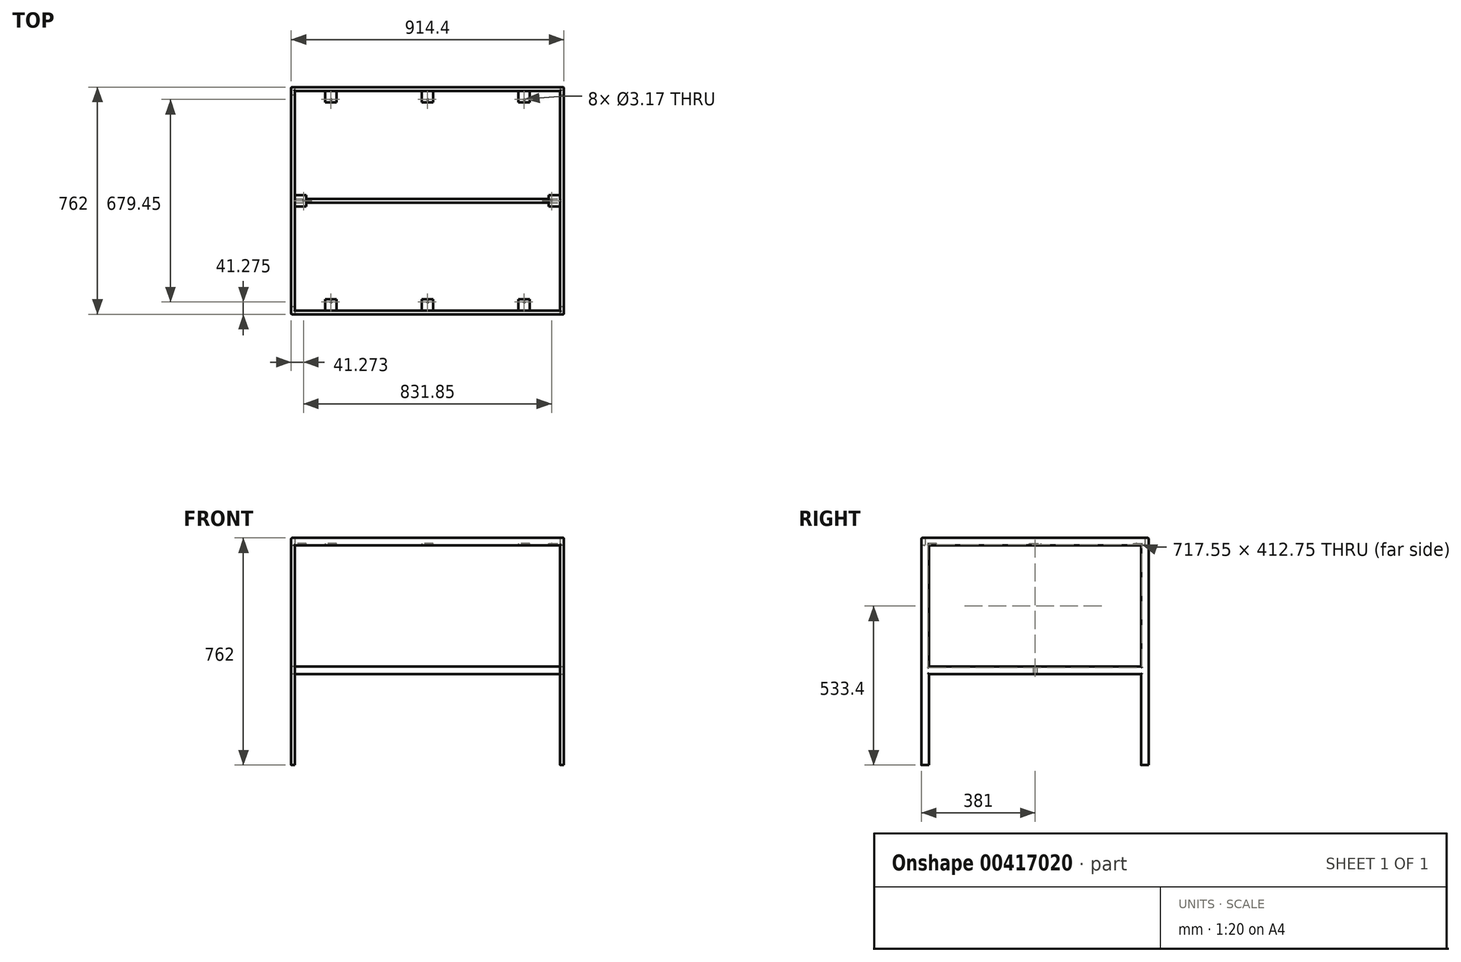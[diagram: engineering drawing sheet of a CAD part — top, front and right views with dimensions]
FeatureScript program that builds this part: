
annotation { "Feature Type Name" : "Feature", "Feature Type Description" : "" }
export const myFeature = defineFeature(function(context is Context, id is Id, definition is map)
    precondition{}
    {
        {
            var Q0;
            Q0=qCreatedBy(makeId("Top.planeOp"),FACE);
            var sketch = newSketch(context, id + "F0", { "sketchPlane" : qUnion([Q0])});
            skLineSegment(sketch, "E0.bottom", {"start": v(-452.22, 494.84) * mm, "end": v(462.18, 494.84) * mm});
            skLineSegment(sketch, "E0.top", {"start": v(-452.22, -267.16) * mm, "end": v(462.18, -267.16) * mm});
            skLineSegment(sketch, "E0.left", {"start": v(-452.22, 494.84) * mm, "end": v(-452.22, -267.16) * mm});
            skLineSegment(sketch, "E0.right", {"start": v(462.18, 494.84) * mm, "end": v(462.18, -267.16) * mm});
            skLineSegment(sketch, "E1.bottom", {"start": v(-439.52, 482.14) * mm, "end": v(449.48, 482.14) * mm});
            skLineSegment(sketch, "E1.top", {"start": v(-439.52, -254.46) * mm, "end": v(449.48, -254.46) * mm});
            skLineSegment(sketch, "E1.left", {"start": v(-439.52, 482.14) * mm, "end": v(-439.52, -254.46) * mm});
            skLineSegment(sketch, "E1.right", {"start": v(449.48, 482.14) * mm, "end": v(449.48, -254.46) * mm});
            skSolve(sketch);
        }
        {
            var Q0;
            Q0=makeQuery(id+"F0.imprint","IMPRINT",FACE,{"disambiguationData":[TD([[makeQuery(id+"F0.imprint","IMPRINT",EDGE,{"derivedFrom":sQuery(id+"F0.wireOp",EDGE,"E0.bottom")}),-1.0]])]});
            extrude(context, id + "F1", {"entities" : qUnion([Q0]), "depth" : 25.4 * mm});
        }
        {
            var Q0;
            Q0=makeQuery(id+"F1.opExtrude","CAP_FACE",FACE,{"disambiguationData":[OSD([sQuery(id+"F0.wireOp",EDGE,"E0.bottom"),sQuery(id+"F0.wireOp",EDGE,"E0.top"),sQuery(id+"F0.wireOp",EDGE,"E0.left"),sQuery(id+"F0.wireOp",EDGE,"E0.right"),sQuery(id+"F0.wireOp",EDGE,"E1.bottom"),sQuery(id+"F0.wireOp",EDGE,"E1.top"),sQuery(id+"F0.wireOp",EDGE,"E1.left"),sQuery(id+"F0.wireOp",EDGE,"E1.right")])],"isStart":true});
            var sketch = newSketch(context, id + "F2", { "sketchPlane" : qUnion([Q0])});
            skLineSegment(sketch, "E2.bottom", {"start": v(-452.22, 267.16) * mm, "end": v(-439.52, 267.16) * mm});
            skLineSegment(sketch, "E2.top", {"start": v(-452.22, 241.76) * mm, "end": v(-439.52, 241.76) * mm});
            skLineSegment(sketch, "E2.left", {"start": v(-452.22, 267.16) * mm, "end": v(-452.22, 241.76) * mm});
            skLineSegment(sketch, "E2.right", {"start": v(-439.52, 267.16) * mm, "end": v(-439.52, 241.76) * mm});
            skLineSegment(sketch, "E3.bottom", {"start": v(-452.22, -494.84) * mm, "end": v(-439.52, -494.84) * mm});
            skLineSegment(sketch, "E3.top", {"start": v(-452.22, -469.44) * mm, "end": v(-439.52, -469.44) * mm});
            skLineSegment(sketch, "E3.left", {"start": v(-452.22, -494.84) * mm, "end": v(-452.22, -469.44) * mm});
            skLineSegment(sketch, "E3.right", {"start": v(-439.52, -494.84) * mm, "end": v(-439.52, -469.44) * mm});
            skLineSegment(sketch, "E4.bottom", {"start": v(462.18, -494.84) * mm, "end": v(449.48, -494.84) * mm});
            skLineSegment(sketch, "E4.top", {"start": v(462.18, -469.44) * mm, "end": v(449.48, -469.44) * mm});
            skLineSegment(sketch, "E4.left", {"start": v(462.18, -494.84) * mm, "end": v(462.18, -469.44) * mm});
            skLineSegment(sketch, "E4.right", {"start": v(449.48, -494.84) * mm, "end": v(449.48, -469.44) * mm});
            skLineSegment(sketch, "E5.bottom", {"start": v(462.18, 267.16) * mm, "end": v(449.48, 267.16) * mm});
            skLineSegment(sketch, "E5.top", {"start": v(462.18, 241.76) * mm, "end": v(449.48, 241.76) * mm});
            skLineSegment(sketch, "E5.left", {"start": v(462.18, 267.16) * mm, "end": v(462.18, 241.76) * mm});
            skLineSegment(sketch, "E5.right", {"start": v(449.48, 267.16) * mm, "end": v(449.48, 241.76) * mm});
            skSolve(sketch);
        }
        {
            var Q0;
            {var subQ2=sQuery(id+"F2.wireOp",EDGE,"E2.bottom");Q0=makeQuery(id+"F2.imprint","IMPRINT",FACE,{"disambiguationData":[TD([[makeQuery(id+"F2.imprint","IMPRINT",EDGE,{"derivedFrom":subQ2}),-1.0]])]});}
            var Q1;
            {var subQ3=sQuery(id+"F2.wireOp",EDGE,"E3.bottom");Q1=makeQuery(id+"F2.imprint","IMPRINT",FACE,{"disambiguationData":[TD([[makeQuery(id+"F2.imprint","IMPRINT",EDGE,{"derivedFrom":subQ3}),1.0]])]});}
            var Q2;
            {var subQ3=sQuery(id+"F2.wireOp",EDGE,"E4.bottom");Q2=makeQuery(id+"F2.imprint","IMPRINT",FACE,{"disambiguationData":[TD([[makeQuery(id+"F2.imprint","IMPRINT",EDGE,{"derivedFrom":subQ3}),1.0]])]});}
            var Q3;
            {var subQ2=sQuery(id+"F2.wireOp",EDGE,"E5.bottom");Q3=makeQuery(id+"F2.imprint","IMPRINT",FACE,{"disambiguationData":[TD([[makeQuery(id+"F2.imprint","IMPRINT",EDGE,{"derivedFrom":subQ2}),-1.0]])]});}
            extrude(context, id + "F3", {"entities" : qUnion([Q0, Q1, Q2, Q3]), "operationType" : NewBodyOperationType.ADD, "depth" : 736.6 * mm});
        }
        {
            var Q0;
            Q0=makeQuery(id+"F3.boolean.opBoolean","MERGE",FACE,{"derivedFrom":[makeQuery(id+"F1.opExtrude","SWEPT_FACE",FACE,{"disambiguationData":[OSD([sQuery(id+"F0.wireOp",EDGE,"E0.right")])]}),makeQuery(id+"F3.opExtrude","SWEPT_FACE",FACE,{"disambiguationData":[OSD([sQuery(id+"F2.wireOp",EDGE,"E4.left")])]}),makeQuery(id+"F3.opExtrude","SWEPT_FACE",FACE,{"disambiguationData":[OSD([sQuery(id+"F2.wireOp",EDGE,"E5.left")])]})]});
            var sketch = newSketch(context, id + "F4", { "sketchPlane" : qUnion([Q0])});
            skLineSegment(sketch, "E6", {"start": v(-241.76, -406.4) * mm, "end": v(469.44, -406.4) * mm});
            skLineSegment(sketch, "E7", {"start": v(-241.76, -431.8) * mm, "end": v(469.44, -431.8) * mm});
            skSolve(sketch);
        }
        {
            var Q0;
            Q0 = qSketchRegion(id + "F4", true);
            var Q1;
            {var subQ0=sQuery(id+"F4.wireOp",EDGE,"E6");Q1=makeQuery(id+"F4.imprint","IMPRINT",FACE,{"disambiguationData":[TD([[makeQuery(id+"F4.imprint","IMPRINT",EDGE,{"derivedFrom":subQ0}),-1.0]])]});}
            extrude(context, id + "F5", {"entities" : qUnion([Q0, Q1]), "operationType" : NewBodyOperationType.ADD, "depth" : -12.7 * mm});
        }
        {
            var Q0;
            Q0=makeQuery(id+"F3.boolean.opBoolean","MERGE",FACE,{"derivedFrom":[makeQuery(id+"F1.opExtrude","SWEPT_FACE",FACE,{"disambiguationData":[OSD([sQuery(id+"F0.wireOp",EDGE,"E0.left")])]}),makeQuery(id+"F3.opExtrude","SWEPT_FACE",FACE,{"disambiguationData":[OSD([sQuery(id+"F2.wireOp",EDGE,"E2.left")])]}),makeQuery(id+"F3.opExtrude","SWEPT_FACE",FACE,{"disambiguationData":[OSD([sQuery(id+"F2.wireOp",EDGE,"E3.left")])]})]});
            var sketch = newSketch(context, id + "F6", { "sketchPlane" : qUnion([Q0])});
            skLineSegment(sketch, "E8", {"start": v(-469.44, -406.4) * mm, "end": v(241.76, -406.4) * mm});
            skLineSegment(sketch, "E9", {"start": v(-469.44, -431.8) * mm, "end": v(241.76, -431.8) * mm});
            skSolve(sketch);
        }
        {
            var Q0;
            Q0 = qSketchRegion(id + "F6", true);
            var Q1;
            {var subQ0=sQuery(id+"F6.wireOp",EDGE,"E8");Q1=makeQuery(id+"F6.imprint","IMPRINT",FACE,{"disambiguationData":[TD([[makeQuery(id+"F6.imprint","IMPRINT",EDGE,{"derivedFrom":subQ0}),-1.0]])]});}
            extrude(context, id + "F7", {"entities" : qUnion([Q0, Q1]), "operationType" : NewBodyOperationType.ADD, "depth" : -12.7 * mm});
        }
        {
            var Q0;
            Q0=makeQuery(id+"F7.opExtrude","SWEPT_FACE",FACE,{"disambiguationData":[OSD([sQuery(id+"F6.wireOp",EDGE,"E9")])]});
            var sketch = newSketch(context, id + "F8", { "sketchPlane" : qUnion([Q0])});
            skLineSegment(sketch, "E10", {"start": v(-439.52, -107.49) * mm, "end": v(449.48, -107.49) * mm});
            skLineSegment(sketch, "E11", {"start": v(-439.52, -120.19) * mm, "end": v(449.48, -120.19) * mm});
            skLineSegment(sketch, "E12", {"start": v(449.48, -107.49) * mm, "end": v(449.48, -120.19) * mm});
            skSolve(sketch);
        }
        {
            var Q0;
            Q0 = qSketchRegion(id + "F8", true);
            var Q1;
            {var subQ0=sQuery(id+"F8.wireOp",EDGE,"E10");Q1=makeQuery(id+"F8.imprint","IMPRINT",FACE,{"disambiguationData":[TD([[makeQuery(id+"F8.imprint","IMPRINT",EDGE,{"derivedFrom":subQ0}),-1.0]])]});}
            extrude(context, id + "F9", {"entities" : qUnion([Q0, Q1]), "operationType" : NewBodyOperationType.ADD, "depth" : -25.4 * mm});
        }
        {
            var Q0;
            Q0=makeQuery(id+"F1.opExtrude","SWEPT_FACE",FACE,{"disambiguationData":[OSD([sQuery(id+"F0.wireOp",EDGE,"E1.top")])]});
            var sketch = newSketch(context, id + "F10", { "sketchPlane" : qUnion([Q0])});
            skLineSegment(sketch, "E13", {"start": v(-347.88, 0) * mm, "end": v(-347.88, 6.35) * mm});
            skLineSegment(sketch, "E14", {"start": v(-347.88, 6.35) * mm, "end": v(-309.78, 6.35) * mm});
            skLineSegment(sketch, "E15", {"start": v(-309.78, 6.35) * mm, "end": v(-309.78, 0) * mm});
            skLineSegment(sketch, "E16", {"start": v(299.82, 0) * mm, "end": v(299.82, 6.35) * mm});
            skLineSegment(sketch, "E17", {"start": v(299.82, 6.35) * mm, "end": v(337.92, 6.35) * mm});
            skLineSegment(sketch, "E18", {"start": v(337.92, 6.35) * mm, "end": v(337.92, 0) * mm});
            skLineSegment(sketch, "E19", {"start": v(-24.03, 0) * mm, "end": v(-24.03, 6.35) * mm});
            skLineSegment(sketch, "E20", {"start": v(-24.03, 6.35) * mm, "end": v(14.07, 6.35) * mm});
            skLineSegment(sketch, "E21", {"start": v(14.07, 6.35) * mm, "end": v(14.07, 0) * mm});
            skSolve(sketch);
        }
        {
            var Q0;
            Q0 = qSketchRegion(id + "F10", true);
            var Q1;
            {var subQ0=sQuery(id+"F10.wireOp",EDGE,"E19");Q1=makeQuery(id+"F10.imprint","IMPRINT",FACE,{"disambiguationData":[TD([[makeQuery(id+"F10.imprint","IMPRINT",EDGE,{"derivedFrom":subQ0}),-1.0]])]});}
            var Q2;
            {var subQ0=sQuery(id+"F10.wireOp",EDGE,"E13");Q2=makeQuery(id+"F10.imprint","IMPRINT",FACE,{"disambiguationData":[TD([[makeQuery(id+"F10.imprint","IMPRINT",EDGE,{"derivedFrom":subQ0}),-1.0]])]});}
            var Q3;
            {var subQ0=sQuery(id+"F10.wireOp",EDGE,"E16");Q3=makeQuery(id+"F10.imprint","IMPRINT",FACE,{"disambiguationData":[TD([[makeQuery(id+"F10.imprint","IMPRINT",EDGE,{"derivedFrom":subQ0}),-1.0]])]});}
            extrude(context, id + "F11", {"entities" : qUnion([Q0, Q1, Q2, Q3]), "operationType" : NewBodyOperationType.ADD, "depth" : 38.1 * mm});
        }
        {
            var Q0;
            Q0=makeQuery(id+"F1.opExtrude","SWEPT_FACE",FACE,{"disambiguationData":[OSD([sQuery(id+"F0.wireOp",EDGE,"E1.bottom")])]});
            var sketch = newSketch(context, id + "F12", { "sketchPlane" : qUnion([Q0])});
            skLineSegment(sketch, "E22", {"start": v(-337.92, 0) * mm, "end": v(-337.92, 6.35) * mm});
            skLineSegment(sketch, "E23", {"start": v(-337.92, 6.35) * mm, "end": v(-299.82, 6.35) * mm});
            skLineSegment(sketch, "E24", {"start": v(-299.82, 6.35) * mm, "end": v(-299.82, 0) * mm});
            skLineSegment(sketch, "E25", {"start": v(-14.07, 0) * mm, "end": v(-14.07, 6.35) * mm});
            skLineSegment(sketch, "E26", {"start": v(-14.07, 6.35) * mm, "end": v(24.03, 6.35) * mm});
            skLineSegment(sketch, "E27", {"start": v(24.03, 6.35) * mm, "end": v(24.03, 0) * mm});
            skLineSegment(sketch, "E28", {"start": v(309.78, 0) * mm, "end": v(309.78, 6.35) * mm});
            skLineSegment(sketch, "E29", {"start": v(309.78, 6.35) * mm, "end": v(347.88, 6.35) * mm});
            skLineSegment(sketch, "E30", {"start": v(347.88, 6.35) * mm, "end": v(347.88, 0) * mm});
            skSolve(sketch);
        }
        {
            var Q0;
            {var subQ0=sQuery(id+"F12.wireOp",EDGE,"E22");Q0=makeQuery(id+"F12.imprint","IMPRINT",FACE,{"disambiguationData":[TD([[makeQuery(id+"F12.imprint","IMPRINT",EDGE,{"derivedFrom":subQ0}),-1.0]])]});}
            var Q1;
            {var subQ0=sQuery(id+"F12.wireOp",EDGE,"E25");Q1=makeQuery(id+"F12.imprint","IMPRINT",FACE,{"disambiguationData":[TD([[makeQuery(id+"F12.imprint","IMPRINT",EDGE,{"derivedFrom":subQ0}),-1.0]])]});}
            var Q2;
            {var subQ0=sQuery(id+"F12.wireOp",EDGE,"E28");Q2=makeQuery(id+"F12.imprint","IMPRINT",FACE,{"disambiguationData":[TD([[makeQuery(id+"F12.imprint","IMPRINT",EDGE,{"derivedFrom":subQ0}),-1.0]])]});}
            extrude(context, id + "F13", {"entities" : qUnion([Q0, Q1, Q2]), "operationType" : NewBodyOperationType.ADD, "depth" : 38.1 * mm});
        }
        {
            var Q0;
            Q0=makeQuery(id+"F7.boolean.opBoolean","MERGE",FACE,{"derivedFrom":[makeQuery(id+"F3.boolean.opBoolean","MERGE",FACE,{"derivedFrom":[makeQuery(id+"F1.opExtrude","SWEPT_FACE",FACE,{"disambiguationData":[OSD([sQuery(id+"F0.wireOp",EDGE,"E1.left")])]}),makeQuery(id+"F3.opExtrude","SWEPT_FACE",FACE,{"disambiguationData":[OSD([sQuery(id+"F2.wireOp",EDGE,"E2.right")])]}),makeQuery(id+"F3.opExtrude","SWEPT_FACE",FACE,{"disambiguationData":[OSD([sQuery(id+"F2.wireOp",EDGE,"E3.right")])]})]}),makeQuery(id+"F7.opExtrude","CAP_FACE",FACE,{"disambiguationData":[OSD([sQuery(id+"F0.wireOp",EDGE,"E0.left"),sQuery(id+"F2.wireOp",EDGE,"E2.top"),sQuery(id+"F2.wireOp",EDGE,"E2.left"),sQuery(id+"F2.wireOp",EDGE,"E3.top"),sQuery(id+"F2.wireOp",EDGE,"E3.left"),sQuery(id+"F6.wireOp",EDGE,"E8"),sQuery(id+"F6.wireOp",EDGE,"E9")])],"isStart":false})]});
            var sketch = newSketch(context, id + "F14", { "sketchPlane" : qUnion([Q0])});
            skLineSegment(sketch, "E31", {"start": v(94.79, 0) * mm, "end": v(94.79, 6.35) * mm});
            skLineSegment(sketch, "E32", {"start": v(94.79, 6.35) * mm, "end": v(132.89, 6.35) * mm});
            skLineSegment(sketch, "E33", {"start": v(132.89, 6.35) * mm, "end": v(132.89, 0) * mm});
            skSolve(sketch);
        }
        {
            var Q0;
            Q0 = qSketchRegion(id + "F14", true);
            var Q1;
            {var subQ0=sQuery(id+"F14.wireOp",EDGE,"E31");Q1=makeQuery(id+"F14.imprint","IMPRINT",FACE,{"disambiguationData":[TD([[makeQuery(id+"F14.imprint","IMPRINT",EDGE,{"derivedFrom":subQ0}),-1.0]])]});}
            extrude(context, id + "F15", {"entities" : qUnion([Q0, Q1]), "operationType" : NewBodyOperationType.ADD, "depth" : 38.1 * mm});
        }
        {
            var Q0;
            Q0=makeQuery(id+"F5.boolean.opBoolean","MERGE",FACE,{"derivedFrom":[makeQuery(id+"F3.boolean.opBoolean","MERGE",FACE,{"derivedFrom":[makeQuery(id+"F1.opExtrude","SWEPT_FACE",FACE,{"disambiguationData":[OSD([sQuery(id+"F0.wireOp",EDGE,"E1.right")])]}),makeQuery(id+"F3.opExtrude","SWEPT_FACE",FACE,{"disambiguationData":[OSD([sQuery(id+"F2.wireOp",EDGE,"E4.right")])]}),makeQuery(id+"F3.opExtrude","SWEPT_FACE",FACE,{"disambiguationData":[OSD([sQuery(id+"F2.wireOp",EDGE,"E5.right")])]})]}),makeQuery(id+"F5.opExtrude","CAP_FACE",FACE,{"disambiguationData":[OSD([sQuery(id+"F0.wireOp",EDGE,"E0.right"),sQuery(id+"F2.wireOp",EDGE,"E4.top"),sQuery(id+"F2.wireOp",EDGE,"E4.left"),sQuery(id+"F2.wireOp",EDGE,"E5.top"),sQuery(id+"F2.wireOp",EDGE,"E5.left"),sQuery(id+"F4.wireOp",EDGE,"E6"),sQuery(id+"F4.wireOp",EDGE,"E7")])],"isStart":false})]});
            var sketch = newSketch(context, id + "F16", { "sketchPlane" : qUnion([Q0])});
            skLineSegment(sketch, "E34", {"start": v(-132.89, 0) * mm, "end": v(-132.89, 6.35) * mm});
            skLineSegment(sketch, "E35", {"start": v(-132.89, 6.35) * mm, "end": v(-94.79, 6.35) * mm});
            skLineSegment(sketch, "E36", {"start": v(-94.79, 6.35) * mm, "end": v(-94.79, 0) * mm});
            skSolve(sketch);
        }
        {
            var Q0;
            {var subQ0=sQuery(id+"F16.wireOp",EDGE,"E34");Q0=makeQuery(id+"F16.imprint","IMPRINT",FACE,{"disambiguationData":[TD([[makeQuery(id+"F16.imprint","IMPRINT",EDGE,{"derivedFrom":subQ0}),-1.0]])]});}
            extrude(context, id + "F17", {"entities" : qUnion([Q0]), "operationType" : NewBodyOperationType.ADD, "depth" : 38.1 * mm});
        }
        {
            var Q0;
            Q0=makeQuery(id+"F13.opExtrude","SWEPT_FACE",FACE,{"disambiguationData":[OSD([sQuery(id+"F12.wireOp",EDGE,"E23")])]});
            var sketch = newSketch(context, id + "F18", { "sketchPlane" : qUnion([Q0])});
            skCircle(sketch, "E37", {"center": v(-318.87, 453.56) * mm, "radius": 1.59 * mm});
            skCircle(sketch, "E38", {"center": v(4.98, 453.56) * mm, "radius": 1.59 * mm});
            skCircle(sketch, "E39", {"center": v(328.83, 453.56) * mm, "radius": 1.59 * mm});
            skCircle(sketch, "E40", {"center": v(-318.87, -225.89) * mm, "radius": 1.59 * mm});
            skCircle(sketch, "E41", {"center": v(4.98, -225.89) * mm, "radius": 1.59 * mm});
            skCircle(sketch, "E42", {"center": v(328.83, -225.89) * mm, "radius": 1.59 * mm});
            skCircle(sketch, "E43", {"center": v(420.9, 113.84) * mm, "radius": 1.59 * mm});
            skCircle(sketch, "E44", {"center": v(-410.95, 113.84) * mm, "radius": 1.59 * mm});
            skSolve(sketch);
        }
        {
            var Q0;
            Q0=makeQuery(id+"F18.imprint","IMPRINT",FACE,{"disambiguationData":[TD([[makeQuery(id+"F18.imprint","IMPRINT",EDGE,{"derivedFrom":sQuery(id+"F18.wireOp",EDGE,"E37")}),1.0]])]});
            var Q1;
            Q1=makeQuery(id+"F18.imprint","IMPRINT",FACE,{"disambiguationData":[TD([[makeQuery(id+"F18.imprint","IMPRINT",EDGE,{"derivedFrom":sQuery(id+"F18.wireOp",EDGE,"E38")}),1.0]])]});
            var Q2;
            Q2=makeQuery(id+"F18.imprint","IMPRINT",FACE,{"disambiguationData":[TD([[makeQuery(id+"F18.imprint","IMPRINT",EDGE,{"derivedFrom":sQuery(id+"F18.wireOp",EDGE,"E39")}),1.0]])]});
            var Q3;
            Q3=makeQuery(id+"F18.imprint","IMPRINT",FACE,{"disambiguationData":[TD([[makeQuery(id+"F18.imprint","IMPRINT",EDGE,{"derivedFrom":sQuery(id+"F18.wireOp",EDGE,"E43")}),1.0]])]});
            var Q4;
            Q4=makeQuery(id+"F18.imprint","IMPRINT",FACE,{"disambiguationData":[TD([[makeQuery(id+"F18.imprint","IMPRINT",EDGE,{"derivedFrom":sQuery(id+"F18.wireOp",EDGE,"E44")}),1.0]])]});
            var Q5;
            Q5=makeQuery(id+"F18.imprint","IMPRINT",FACE,{"disambiguationData":[TD([[makeQuery(id+"F18.imprint","IMPRINT",EDGE,{"derivedFrom":sQuery(id+"F18.wireOp",EDGE,"E40")}),1.0]])]});
            var Q6;
            Q6=makeQuery(id+"F18.imprint","IMPRINT",FACE,{"disambiguationData":[TD([[makeQuery(id+"F18.imprint","IMPRINT",EDGE,{"derivedFrom":sQuery(id+"F18.wireOp",EDGE,"E41")}),1.0]])]});
            var Q7;
            Q7=makeQuery(id+"F18.imprint","IMPRINT",FACE,{"disambiguationData":[TD([[makeQuery(id+"F18.imprint","IMPRINT",EDGE,{"derivedFrom":sQuery(id+"F18.wireOp",EDGE,"E42")}),1.0]])]});
            extrude(context, id + "F19", {"entities" : qUnion([Q0, Q1, Q2, Q3, Q4, Q5, Q6, Q7]), "operationType" : NewBodyOperationType.REMOVE, "endBound" : BoundingType.UP_TO_NEXT, "oppositeDirection" : true, "depth" : 25.4 * mm});
        }
        {
            var Q0;
            {var subQ0=sQuery(id+"F2.wireOp",EDGE,"E3.top");var subQ2=sQuery(id+"F0.wireOp",EDGE,"E0.left");var subQ3=sQuery(id+"F6.wireOp",EDGE,"E8");var subQ4=sQuery(id+"F2.wireOp",EDGE,"E3.left");Q0=makeQuery(id+"F7.boolean.opBoolean","SPLIT",EDGE,{"disambiguationData":[TD([makeQuery(id+"F7.opExtrude","SWEPT_FACE",FACE,{"disambiguationData":[OSD([subQ3])]})])],"derivedFrom":makeQuery(id+"F3.opExtrude","SWEPT_EDGE",EDGE,{"disambiguationData":[OSD([subQ2,subQ0,subQ4])]})});}
            var Q1;
            {var subQ0=sQuery(id+"F2.wireOp",EDGE,"E3.left");var subQ1=sQuery(id+"F2.wireOp",EDGE,"E3.top");var subQ3=sQuery(id+"F0.wireOp",EDGE,"E0.left");var subQ4=sQuery(id+"F6.wireOp",EDGE,"E9");Q1=makeQuery(id+"F7.boolean.opBoolean","SPLIT",EDGE,{"disambiguationData":[TD([makeQuery(id+"F7.opExtrude","SWEPT_FACE",FACE,{"disambiguationData":[OSD([subQ4])]})])],"derivedFrom":makeQuery(id+"F3.opExtrude","SWEPT_EDGE",EDGE,{"disambiguationData":[OSD([subQ3,subQ1,subQ0])]})});}
            var Q2;
            {var subQ0=sQuery(id+"F2.wireOp",EDGE,"E3.top");var subQ1=sQuery(id+"F2.wireOp",EDGE,"E3.right");var subQ3=sQuery(id+"F0.wireOp",EDGE,"E1.left");var subQ4=sQuery(id+"F6.wireOp",EDGE,"E9");Q2=makeQuery(id+"F7.boolean.opBoolean","SPLIT",EDGE,{"disambiguationData":[TD([makeQuery(id+"F7.opExtrude","SWEPT_FACE",FACE,{"disambiguationData":[OSD([subQ4])]})])],"derivedFrom":makeQuery(id+"F3.opExtrude","SWEPT_EDGE",EDGE,{"disambiguationData":[OSD([subQ3,subQ0,subQ1])]})});}
            var Q3;
            {var subQ0=sQuery(id+"F2.wireOp",EDGE,"E3.top");var subQ1=sQuery(id+"F0.wireOp",EDGE,"E1.left");var subQ3=sQuery(id+"F2.wireOp",EDGE,"E3.right");var subQ4=sQuery(id+"F6.wireOp",EDGE,"E8");Q3=makeQuery(id+"F7.boolean.opBoolean","SPLIT",EDGE,{"disambiguationData":[TD([makeQuery(id+"F7.opExtrude","SWEPT_FACE",FACE,{"disambiguationData":[OSD([subQ4])]})])],"derivedFrom":makeQuery(id+"F3.opExtrude","SWEPT_EDGE",EDGE,{"disambiguationData":[OSD([subQ1,subQ0,subQ3])]})});}
            var Q4;
            Q4=makeQuery(id+"F7.opExtrude","CAP_EDGE",EDGE,{"disambiguationData":[OSD([sQuery(id+"F6.wireOp",EDGE,"E8")])],"isStart":true});
            var Q5;
            Q5=makeQuery(id+"F7.opExtrude","CAP_EDGE",EDGE,{"disambiguationData":[OSD([sQuery(id+"F6.wireOp",EDGE,"E9")])],"isStart":true});
            var Q6;
            {var subQ0=sQuery(id+"F2.wireOp",EDGE,"E2.left");var subQ1=sQuery(id+"F2.wireOp",EDGE,"E2.top");var subQ2=sQuery(id+"F0.wireOp",EDGE,"E0.left");var subQ3=sQuery(id+"F6.wireOp",EDGE,"E9");Q6=makeQuery(id+"F7.boolean.opBoolean","SPLIT",EDGE,{"disambiguationData":[TD([makeQuery(id+"F7.opExtrude","SWEPT_FACE",FACE,{"disambiguationData":[OSD([subQ3])]})])],"derivedFrom":makeQuery(id+"F3.opExtrude","SWEPT_EDGE",EDGE,{"disambiguationData":[OSD([subQ2,subQ1,subQ0])]})});}
            var Q7;
            {var subQ0=sQuery(id+"F2.wireOp",EDGE,"E2.left");var subQ1=sQuery(id+"F0.wireOp",EDGE,"E0.left");var subQ2=sQuery(id+"F2.wireOp",EDGE,"E2.top");var subQ3=sQuery(id+"F6.wireOp",EDGE,"E8");Q7=makeQuery(id+"F7.boolean.opBoolean","SPLIT",EDGE,{"disambiguationData":[TD([makeQuery(id+"F7.opExtrude","SWEPT_FACE",FACE,{"disambiguationData":[OSD([subQ3])]})])],"derivedFrom":makeQuery(id+"F3.opExtrude","SWEPT_EDGE",EDGE,{"disambiguationData":[OSD([subQ1,subQ2,subQ0])]})});}
            var Q8;
            Q8=makeQuery(id+"F1.opExtrude","CAP_EDGE",EDGE,{"disambiguationData":[OSD([sQuery(id+"F0.wireOp",EDGE,"E0.left")])],"isStart":true});
            fillet(context, id + "F20", {"entities" : qUnion([Q0, Q1, Q2, Q3, Q4, Q5, Q6, Q7, Q8]), "radius" : 3.17 * mm, "tangentPropagation" : true, "allowEdgeOverflow" : false});
        }
        {
            var Q0;
            Q0=makeQuery(id+"F3.opExtrude","SWEPT_EDGE",EDGE,{"disambiguationData":[OSD([sQuery(id+"F0.wireOp",EDGE,"E0.top"),sQuery(id+"F2.wireOp",EDGE,"E2.bottom"),sQuery(id+"F2.wireOp",EDGE,"E2.right")])]});
            var Q1;
            Q1=makeQuery(id+"F1.opExtrude","CAP_EDGE",EDGE,{"disambiguationData":[OSD([sQuery(id+"F0.wireOp",EDGE,"E0.top")])],"isStart":true});
            var Q2;
            Q2=makeQuery(id+"F3.opExtrude","SWEPT_EDGE",EDGE,{"disambiguationData":[OSD([sQuery(id+"F0.wireOp",EDGE,"E0.top"),sQuery(id+"F2.wireOp",EDGE,"E5.bottom"),sQuery(id+"F2.wireOp",EDGE,"E5.right")])]});
            var Q3;
            {var subQ0=sQuery(id+"F2.wireOp",EDGE,"E2.top");var subQ1=sQuery(id+"F6.wireOp",EDGE,"E8");Q3=makeQuery(id+"F9.boolean.opBoolean","SPLIT",EDGE,{"disambiguationData":[TD([makeQuery(id+"F3.opExtrude","SWEPT_FACE",FACE,{"disambiguationData":[OSD([subQ0])]})])],"derivedFrom":makeQuery(id+"F7.opExtrude","CAP_EDGE",EDGE,{"disambiguationData":[OSD([subQ1])],"isStart":false})});}
            var Q4;
            {var subQ0=sQuery(id+"F2.wireOp",EDGE,"E2.top");var subQ2=sQuery(id+"F6.wireOp",EDGE,"E9");Q4=makeQuery(id+"F9.boolean.opBoolean","SPLIT",EDGE,{"disambiguationData":[TD([makeQuery(id+"F3.opExtrude","SWEPT_FACE",FACE,{"disambiguationData":[OSD([subQ0])]})])],"derivedFrom":makeQuery(id+"F7.opExtrude","CAP_EDGE",EDGE,{"disambiguationData":[OSD([subQ2])],"isStart":false})});}
            var Q5;
            {var subQ0=sQuery(id+"F2.wireOp",EDGE,"E3.top");var subQ2=sQuery(id+"F6.wireOp",EDGE,"E8");Q5=makeQuery(id+"F9.boolean.opBoolean","SPLIT",EDGE,{"disambiguationData":[TD([makeQuery(id+"F3.opExtrude","SWEPT_FACE",FACE,{"disambiguationData":[OSD([subQ0])]})])],"derivedFrom":makeQuery(id+"F7.opExtrude","CAP_EDGE",EDGE,{"disambiguationData":[OSD([subQ2])],"isStart":false})});}
            var Q6;
            {var subQ0=sQuery(id+"F2.wireOp",EDGE,"E3.top");var subQ2=sQuery(id+"F6.wireOp",EDGE,"E9");Q6=makeQuery(id+"F9.boolean.opBoolean","SPLIT",EDGE,{"disambiguationData":[TD([makeQuery(id+"F3.opExtrude","SWEPT_FACE",FACE,{"disambiguationData":[OSD([subQ0])]})])],"derivedFrom":makeQuery(id+"F7.opExtrude","CAP_EDGE",EDGE,{"disambiguationData":[OSD([subQ2])],"isStart":false})});}
            fillet(context, id + "F21", {"entities" : qUnion([Q0, Q1, Q2, Q3, Q4, Q5, Q6]), "radius" : 3.17 * mm, "tangentPropagation" : true, "allowEdgeOverflow" : false});
        }
        {
            var Q0;
            Q0=makeQuery(id+"F9.opExtrude","CAP_EDGE",EDGE,{"disambiguationData":[OSD([sQuery(id+"F8.wireOp",EDGE,"E10")])],"isStart":false});
            var Q1;
            Q1=makeQuery(id+"F9.opExtrude","CAP_EDGE",EDGE,{"disambiguationData":[OSD([sQuery(id+"F8.wireOp",EDGE,"E10")])],"isStart":true});
            fillet(context, id + "F22", {"entities" : qUnion([Q0, Q1]), "radius" : 3.17 * mm, "tangentPropagation" : true, "allowEdgeOverflow" : false});
        }
        {
            var Q0;
            {var subQ0=sQuery(id+"F2.wireOp",EDGE,"E4.left");var subQ1=sQuery(id+"F2.wireOp",EDGE,"E4.top");var subQ2=sQuery(id+"F0.wireOp",EDGE,"E0.right");var subQ4=sQuery(id+"F4.wireOp",EDGE,"E7");Q0=makeQuery(id+"F5.boolean.opBoolean","SPLIT",EDGE,{"disambiguationData":[TD([makeQuery(id+"F5.opExtrude","SWEPT_FACE",FACE,{"disambiguationData":[OSD([subQ4])]})])],"derivedFrom":makeQuery(id+"F3.opExtrude","SWEPT_EDGE",EDGE,{"disambiguationData":[OSD([subQ2,subQ1,subQ0])]})});}
            var Q1;
            {var subQ0=sQuery(id+"F2.wireOp",EDGE,"E4.right");var subQ1=sQuery(id+"F2.wireOp",EDGE,"E4.top");var subQ3=sQuery(id+"F0.wireOp",EDGE,"E1.right");var subQ4=sQuery(id+"F4.wireOp",EDGE,"E7");Q1=makeQuery(id+"F5.boolean.opBoolean","SPLIT",EDGE,{"disambiguationData":[TD([makeQuery(id+"F5.opExtrude","SWEPT_FACE",FACE,{"disambiguationData":[OSD([subQ4])]})])],"derivedFrom":makeQuery(id+"F3.opExtrude","SWEPT_EDGE",EDGE,{"disambiguationData":[OSD([subQ3,subQ1,subQ0])]})});}
            var Q2;
            {var subQ0=sQuery(id+"F2.wireOp",EDGE,"E4.right");var subQ1=sQuery(id+"F2.wireOp",EDGE,"E4.top");var subQ2=sQuery(id+"F0.wireOp",EDGE,"E1.right");var subQ4=sQuery(id+"F4.wireOp",EDGE,"E6");Q2=makeQuery(id+"F5.boolean.opBoolean","SPLIT",EDGE,{"disambiguationData":[TD([makeQuery(id+"F5.opExtrude","SWEPT_FACE",FACE,{"disambiguationData":[OSD([subQ4])]})])],"derivedFrom":makeQuery(id+"F3.opExtrude","SWEPT_EDGE",EDGE,{"disambiguationData":[OSD([subQ2,subQ1,subQ0])]})});}
            var Q3;
            {var subQ0=sQuery(id+"F2.wireOp",EDGE,"E4.left");var subQ1=sQuery(id+"F4.wireOp",EDGE,"E6");var subQ2=sQuery(id+"F2.wireOp",EDGE,"E4.top");var subQ3=sQuery(id+"F0.wireOp",EDGE,"E0.right");Q3=makeQuery(id+"F5.boolean.opBoolean","SPLIT",EDGE,{"disambiguationData":[TD([makeQuery(id+"F5.opExtrude","SWEPT_FACE",FACE,{"disambiguationData":[OSD([subQ1])]})])],"derivedFrom":makeQuery(id+"F3.opExtrude","SWEPT_EDGE",EDGE,{"disambiguationData":[OSD([subQ3,subQ2,subQ0])]})});}
            var Q4;
            {var subQ0=sQuery(id+"F2.wireOp",EDGE,"E5.top");var subQ2=sQuery(id+"F4.wireOp",EDGE,"E6");var subQ3=sQuery(id+"F0.wireOp",EDGE,"E0.right");var subQ4=sQuery(id+"F2.wireOp",EDGE,"E5.left");Q4=makeQuery(id+"F5.boolean.opBoolean","SPLIT",EDGE,{"disambiguationData":[TD([makeQuery(id+"F5.opExtrude","SWEPT_FACE",FACE,{"disambiguationData":[OSD([subQ2])]})])],"derivedFrom":makeQuery(id+"F3.opExtrude","SWEPT_EDGE",EDGE,{"disambiguationData":[OSD([subQ3,subQ0,subQ4])]})});}
            var Q5;
            {var subQ0=sQuery(id+"F2.wireOp",EDGE,"E5.top");var subQ1=sQuery(id+"F0.wireOp",EDGE,"E1.right");var subQ3=sQuery(id+"F2.wireOp",EDGE,"E5.right");var subQ4=sQuery(id+"F4.wireOp",EDGE,"E6");Q5=makeQuery(id+"F5.boolean.opBoolean","SPLIT",EDGE,{"disambiguationData":[TD([makeQuery(id+"F5.opExtrude","SWEPT_FACE",FACE,{"disambiguationData":[OSD([subQ4])]})])],"derivedFrom":makeQuery(id+"F3.opExtrude","SWEPT_EDGE",EDGE,{"disambiguationData":[OSD([subQ1,subQ0,subQ3])]})});}
            var Q6;
            {var subQ0=sQuery(id+"F2.wireOp",EDGE,"E5.left");var subQ1=sQuery(id+"F2.wireOp",EDGE,"E5.top");var subQ3=sQuery(id+"F0.wireOp",EDGE,"E0.right");var subQ4=sQuery(id+"F4.wireOp",EDGE,"E7");Q6=makeQuery(id+"F5.boolean.opBoolean","SPLIT",EDGE,{"disambiguationData":[TD([makeQuery(id+"F5.opExtrude","SWEPT_FACE",FACE,{"disambiguationData":[OSD([subQ4])]})])],"derivedFrom":makeQuery(id+"F3.opExtrude","SWEPT_EDGE",EDGE,{"disambiguationData":[OSD([subQ3,subQ1,subQ0])]})});}
            var Q7;
            {var subQ0=sQuery(id+"F2.wireOp",EDGE,"E5.right");var subQ2=sQuery(id+"F2.wireOp",EDGE,"E5.top");var subQ3=sQuery(id+"F0.wireOp",EDGE,"E1.right");var subQ4=sQuery(id+"F4.wireOp",EDGE,"E7");Q7=makeQuery(id+"F5.boolean.opBoolean","SPLIT",EDGE,{"disambiguationData":[TD([makeQuery(id+"F5.opExtrude","SWEPT_FACE",FACE,{"disambiguationData":[OSD([subQ4])]})])],"derivedFrom":makeQuery(id+"F3.opExtrude","SWEPT_EDGE",EDGE,{"disambiguationData":[OSD([subQ3,subQ2,subQ0])]})});}
            var Q8;
            Q8=makeQuery(id+"F5.opExtrude","CAP_EDGE",EDGE,{"disambiguationData":[OSD([sQuery(id+"F4.wireOp",EDGE,"E7")])],"isStart":true});
            var Q9;
            Q9=makeQuery(id+"F5.opExtrude","CAP_EDGE",EDGE,{"disambiguationData":[OSD([sQuery(id+"F4.wireOp",EDGE,"E6")])],"isStart":true});
            var Q10;
            Q10=makeQuery(id+"F1.opExtrude","CAP_EDGE",EDGE,{"disambiguationData":[OSD([sQuery(id+"F0.wireOp",EDGE,"E0.right")])],"isStart":true});
            fillet(context, id + "F23", {"entities" : qUnion([Q0, Q1, Q2, Q3, Q4, Q5, Q6, Q7, Q8, Q9, Q10]), "radius" : 3.17 * mm, "tangentPropagation" : true, "allowEdgeOverflow" : false});
        }
        {
            var Q0;
            Q0=makeQuery(id+"F1.opExtrude","CAP_EDGE",EDGE,{"disambiguationData":[OSD([sQuery(id+"F0.wireOp",EDGE,"E0.bottom")])],"isStart":true});
            var Q1;
            Q1=makeQuery(id+"F3.opExtrude","SWEPT_EDGE",EDGE,{"disambiguationData":[OSD([sQuery(id+"F0.wireOp",EDGE,"E0.bottom"),sQuery(id+"F2.wireOp",EDGE,"E4.bottom"),sQuery(id+"F2.wireOp",EDGE,"E4.right")])]});
            var Q2;
            Q2=makeQuery(id+"F3.boolean.opBoolean","MERGE",EDGE,{"derivedFrom":[makeQuery(id+"F1.opExtrude","SWEPT_EDGE",EDGE,{"disambiguationData":[OSD([sQuery(id+"F0.wireOp",EDGE,"E0.bottom"),sQuery(id+"F0.wireOp",EDGE,"E0.right")])]}),makeQuery(id+"F3.opExtrude","SWEPT_EDGE",EDGE,{"disambiguationData":[OSD([sQuery(id+"F2.wireOp",EDGE,"E4.bottom"),sQuery(id+"F2.wireOp",EDGE,"E4.left")])]})]});
            var Q3;
            Q3=makeQuery(id+"F3.opExtrude","SWEPT_EDGE",EDGE,{"disambiguationData":[OSD([sQuery(id+"F0.wireOp",EDGE,"E0.bottom"),sQuery(id+"F2.wireOp",EDGE,"E3.bottom"),sQuery(id+"F2.wireOp",EDGE,"E3.right")])]});
            var Q4;
            Q4=makeQuery(id+"F3.boolean.opBoolean","MERGE",EDGE,{"derivedFrom":[makeQuery(id+"F1.opExtrude","SWEPT_EDGE",EDGE,{"disambiguationData":[OSD([sQuery(id+"F0.wireOp",EDGE,"E0.bottom"),sQuery(id+"F0.wireOp",EDGE,"E0.left")])]}),makeQuery(id+"F3.opExtrude","SWEPT_EDGE",EDGE,{"disambiguationData":[OSD([sQuery(id+"F2.wireOp",EDGE,"E3.bottom"),sQuery(id+"F2.wireOp",EDGE,"E3.left")])]})]});
            fillet(context, id + "F24", {"entities" : qUnion([Q0, Q1, Q2, Q3, Q4]), "radius" : 3.17 * mm, "tangentPropagation" : true, "allowEdgeOverflow" : false});
        }
        {
            var Q0;
            Q0=makeQuery(id+"F9.opExtrude","CAP_EDGE",EDGE,{"disambiguationData":[OSD([sQuery(id+"F8.wireOp",EDGE,"E11")])],"isStart":false});
            var Q1;
            Q1=makeQuery(id+"F9.opExtrude","CAP_EDGE",EDGE,{"disambiguationData":[OSD([sQuery(id+"F8.wireOp",EDGE,"E11")])],"isStart":true});
            var Q2;
            {var subQ1=sQuery(id+"F2.wireOp",EDGE,"E4.top");var subQ2=sQuery(id+"F4.wireOp",EDGE,"E6");Q2=makeQuery(id+"F9.boolean.opBoolean","SPLIT",EDGE,{"disambiguationData":[TD([makeQuery(id+"F3.opExtrude","SWEPT_FACE",FACE,{"disambiguationData":[OSD([subQ1])]})])],"derivedFrom":makeQuery(id+"F5.opExtrude","CAP_EDGE",EDGE,{"disambiguationData":[OSD([subQ2])],"isStart":false})});}
            var Q3;
            {var subQ0=sQuery(id+"F2.wireOp",EDGE,"E4.top");var subQ1=sQuery(id+"F4.wireOp",EDGE,"E7");Q3=makeQuery(id+"F9.boolean.opBoolean","SPLIT",EDGE,{"disambiguationData":[TD([makeQuery(id+"F3.opExtrude","SWEPT_FACE",FACE,{"disambiguationData":[OSD([subQ0])]})])],"derivedFrom":makeQuery(id+"F5.opExtrude","CAP_EDGE",EDGE,{"disambiguationData":[OSD([subQ1])],"isStart":false})});}
            var Q4;
            {var subQ1=sQuery(id+"F2.wireOp",EDGE,"E5.top");var subQ2=sQuery(id+"F4.wireOp",EDGE,"E6");Q4=makeQuery(id+"F9.boolean.opBoolean","SPLIT",EDGE,{"disambiguationData":[TD([makeQuery(id+"F3.opExtrude","SWEPT_FACE",FACE,{"disambiguationData":[OSD([subQ1])]})])],"derivedFrom":makeQuery(id+"F5.opExtrude","CAP_EDGE",EDGE,{"disambiguationData":[OSD([subQ2])],"isStart":false})});}
            var Q5;
            {var subQ0=sQuery(id+"F2.wireOp",EDGE,"E5.top");var subQ1=sQuery(id+"F4.wireOp",EDGE,"E7");Q5=makeQuery(id+"F9.boolean.opBoolean","SPLIT",EDGE,{"disambiguationData":[TD([makeQuery(id+"F3.opExtrude","SWEPT_FACE",FACE,{"disambiguationData":[OSD([subQ0])]})])],"derivedFrom":makeQuery(id+"F5.opExtrude","CAP_EDGE",EDGE,{"disambiguationData":[OSD([subQ1])],"isStart":false})});}
            fillet(context, id + "F25", {"entities" : qUnion([Q0, Q1, Q2, Q3, Q4, Q5]), "radius" : 3.17 * mm, "tangentPropagation" : true, "allowEdgeOverflow" : false});
        }
        {
            var Q0;
            Q0=makeQuery(id+"F3.boolean.opBoolean","MERGE",EDGE,{"derivedFrom":[makeQuery(id+"F1.opExtrude","SWEPT_EDGE",EDGE,{"disambiguationData":[OSD([sQuery(id+"F0.wireOp",EDGE,"E0.top"),sQuery(id+"F0.wireOp",EDGE,"E0.right")])]}),makeQuery(id+"F3.opExtrude","SWEPT_EDGE",EDGE,{"disambiguationData":[OSD([sQuery(id+"F2.wireOp",EDGE,"E5.bottom"),sQuery(id+"F2.wireOp",EDGE,"E5.left")])]})]});
            var Q1;
            Q1=makeQuery(id+"F1.opExtrude","CAP_EDGE",EDGE,{"disambiguationData":[OSD([sQuery(id+"F0.wireOp",EDGE,"E0.right")])],"isStart":false});
            var Q2;
            Q2=makeQuery(id+"F1.opExtrude","CAP_EDGE",EDGE,{"disambiguationData":[OSD([sQuery(id+"F0.wireOp",EDGE,"E1.right")])],"isStart":false});
            var Q3;
            Q3=makeQuery(id+"F1.opExtrude","CAP_EDGE",EDGE,{"disambiguationData":[OSD([sQuery(id+"F0.wireOp",EDGE,"E0.top")])],"isStart":false});
            var Q4;
            Q4=makeQuery(id+"F1.opExtrude","CAP_EDGE",EDGE,{"disambiguationData":[OSD([sQuery(id+"F0.wireOp",EDGE,"E1.top")])],"isStart":false});
            var Q5;
            Q5=makeQuery(id+"F1.opExtrude","CAP_EDGE",EDGE,{"disambiguationData":[OSD([sQuery(id+"F0.wireOp",EDGE,"E1.bottom")])],"isStart":false});
            var Q6;
            Q6=makeQuery(id+"F1.opExtrude","CAP_EDGE",EDGE,{"disambiguationData":[OSD([sQuery(id+"F0.wireOp",EDGE,"E0.bottom")])],"isStart":false});
            fillet(context, id + "F26", {"entities" : qUnion([Q0, Q1, Q2, Q3, Q4, Q5, Q6]), "radius" : 3.17 * mm, "tangentPropagation" : true, "allowEdgeOverflow" : false});
        }
        {
            var Q0;
            {var subQ0=sQuery(id+"F2.wireOp",EDGE,"E5.top");var subQ1=sQuery(id+"F0.wireOp",EDGE,"E1.right");Q0=makeQuery(id+"F17.boolean.opBoolean","SPLIT",EDGE,{"disambiguationData":[TD([makeQuery(id+"F3.opExtrude","SWEPT_FACE",FACE,{"disambiguationData":[OSD([subQ0])]})])],"derivedFrom":makeQuery(id+"F1.opExtrude","CAP_EDGE",EDGE,{"disambiguationData":[OSD([subQ1])],"isStart":true})});}
            var Q1;
            {var subQ0=sQuery(id+"F2.wireOp",EDGE,"E4.top");var subQ1=sQuery(id+"F0.wireOp",EDGE,"E1.right");Q1=makeQuery(id+"F17.boolean.opBoolean","SPLIT",EDGE,{"disambiguationData":[TD([makeQuery(id+"F3.opExtrude","SWEPT_FACE",FACE,{"disambiguationData":[OSD([subQ0])]})])],"derivedFrom":makeQuery(id+"F1.opExtrude","CAP_EDGE",EDGE,{"disambiguationData":[OSD([subQ1])],"isStart":true})});}
            var Q2;
            {var subQ0=sQuery(id+"F0.wireOp",EDGE,"E1.top");var subQ1=sQuery(id+"F0.wireOp",EDGE,"E1.right");var subQ4=makeQuery(id+"F1.opExtrude","CAP_EDGE",EDGE,{"disambiguationData":[OSD([subQ0])],"isStart":true});Q2=makeQuery(id+"F11.boolean.opBoolean","SPLIT",EDGE,{"disambiguationData":[TD([makeQuery(id+"F1.opExtrude","SWEPT_FACE",FACE,{"disambiguationData":[OSD([subQ1])]})])],"derivedFrom":subQ4});}
            var Q3;
            {var subQ1=sQuery(id+"F10.wireOp",EDGE,"E15");var subQ2=sQuery(id+"F0.wireOp",EDGE,"E1.top");var subQ3=makeQuery(id+"F1.opExtrude","CAP_EDGE",EDGE,{"disambiguationData":[OSD([subQ2])],"isStart":true});Q3=makeQuery(id+"F11.boolean.opBoolean","SPLIT",EDGE,{"disambiguationData":[TD([makeQuery(id+"F11.opExtrude","SWEPT_FACE",FACE,{"disambiguationData":[OSD([subQ1])]})])],"derivedFrom":subQ3});}
            var Q4;
            {var subQ1=sQuery(id+"F12.wireOp",EDGE,"E27");var subQ2=sQuery(id+"F0.wireOp",EDGE,"E1.bottom");var subQ3=makeQuery(id+"F1.opExtrude","CAP_EDGE",EDGE,{"disambiguationData":[OSD([subQ2])],"isStart":true});Q4=makeQuery(id+"F13.boolean.opBoolean","SPLIT",EDGE,{"disambiguationData":[TD([makeQuery(id+"F13.opExtrude","SWEPT_FACE",FACE,{"disambiguationData":[OSD([subQ1])]})])],"derivedFrom":subQ3});}
            var Q5;
            {var subQ1=sQuery(id+"F0.wireOp",EDGE,"E1.right");var subQ2=sQuery(id+"F0.wireOp",EDGE,"E1.bottom");var subQ3=makeQuery(id+"F1.opExtrude","CAP_EDGE",EDGE,{"disambiguationData":[OSD([subQ2])],"isStart":true});Q5=makeQuery(id+"F13.boolean.opBoolean","SPLIT",EDGE,{"disambiguationData":[TD([makeQuery(id+"F1.opExtrude","SWEPT_FACE",FACE,{"disambiguationData":[OSD([subQ1])]})])],"derivedFrom":subQ3});}
            var Q6;
            {var subQ1=sQuery(id+"F0.wireOp",EDGE,"E1.bottom");var subQ2=makeQuery(id+"F1.opExtrude","CAP_EDGE",EDGE,{"disambiguationData":[OSD([subQ1])],"isStart":true});var subQ3=sQuery(id+"F12.wireOp",EDGE,"E24");Q6=makeQuery(id+"F13.boolean.opBoolean","SPLIT",EDGE,{"disambiguationData":[TD([makeQuery(id+"F13.opExtrude","SWEPT_FACE",FACE,{"disambiguationData":[OSD([subQ3])]})])],"derivedFrom":subQ2});}
            var Q7;
            {var subQ0=sQuery(id+"F0.wireOp",EDGE,"E1.bottom");var subQ1=sQuery(id+"F0.wireOp",EDGE,"E1.left");var subQ3=makeQuery(id+"F1.opExtrude","CAP_EDGE",EDGE,{"disambiguationData":[OSD([subQ0])],"isStart":true});Q7=makeQuery(id+"F13.boolean.opBoolean","SPLIT",EDGE,{"disambiguationData":[TD([makeQuery(id+"F1.opExtrude","SWEPT_FACE",FACE,{"disambiguationData":[OSD([subQ1])]})])],"derivedFrom":subQ3});}
            var Q8;
            {var subQ0=sQuery(id+"F2.wireOp",EDGE,"E3.top");var subQ1=sQuery(id+"F0.wireOp",EDGE,"E1.left");Q8=makeQuery(id+"F15.boolean.opBoolean","SPLIT",EDGE,{"disambiguationData":[TD([makeQuery(id+"F3.opExtrude","SWEPT_FACE",FACE,{"disambiguationData":[OSD([subQ0])]})])],"derivedFrom":makeQuery(id+"F1.opExtrude","CAP_EDGE",EDGE,{"disambiguationData":[OSD([subQ1])],"isStart":true})});}
            var Q9;
            {var subQ0=sQuery(id+"F0.wireOp",EDGE,"E1.left");var subQ1=sQuery(id+"F2.wireOp",EDGE,"E2.top");Q9=makeQuery(id+"F15.boolean.opBoolean","SPLIT",EDGE,{"disambiguationData":[TD([makeQuery(id+"F3.opExtrude","SWEPT_FACE",FACE,{"disambiguationData":[OSD([subQ1])]})])],"derivedFrom":makeQuery(id+"F1.opExtrude","CAP_EDGE",EDGE,{"disambiguationData":[OSD([subQ0])],"isStart":true})});}
            var Q10;
            {var subQ0=sQuery(id+"F0.wireOp",EDGE,"E1.left");var subQ2=sQuery(id+"F0.wireOp",EDGE,"E1.top");var subQ4=makeQuery(id+"F1.opExtrude","CAP_EDGE",EDGE,{"disambiguationData":[OSD([subQ2])],"isStart":true});Q10=makeQuery(id+"F11.boolean.opBoolean","SPLIT",EDGE,{"disambiguationData":[TD([makeQuery(id+"F1.opExtrude","SWEPT_FACE",FACE,{"disambiguationData":[OSD([subQ0])]})])],"derivedFrom":subQ4});}
            var Q11;
            {var subQ1=sQuery(id+"F10.wireOp",EDGE,"E16");var subQ2=sQuery(id+"F0.wireOp",EDGE,"E1.top");var subQ3=makeQuery(id+"F1.opExtrude","CAP_EDGE",EDGE,{"disambiguationData":[OSD([subQ2])],"isStart":true});Q11=makeQuery(id+"F11.boolean.opBoolean","SPLIT",EDGE,{"disambiguationData":[TD([makeQuery(id+"F11.opExtrude","SWEPT_FACE",FACE,{"disambiguationData":[OSD([subQ1])]})])],"derivedFrom":subQ3});}
            fillet(context, id + "F27", {"entities" : qUnion([Q0, Q1, Q2, Q3, Q4, Q5, Q6, Q7, Q8, Q9, Q10, Q11]), "radius" : 3.17 * mm, "tangentPropagation" : true, "allowEdgeOverflow" : false});
        }
        {
            var Q0;
            Q0=makeQuery(id+"F1.opExtrude","CAP_EDGE",EDGE,{"disambiguationData":[OSD([sQuery(id+"F0.wireOp",EDGE,"E1.left")])],"isStart":false});
            fillet(context, id + "F28", {"entities" : qUnion([Q0]), "radius" : 3.17 * mm, "tangentPropagation" : true, "allowEdgeOverflow" : false});
        }
        {
            var Q0;
            {var subQ0=sQuery(id+"F2.wireOp",EDGE,"E2.right");var subQ1=sQuery(id+"F0.wireOp",EDGE,"E1.left");var subQ2=sQuery(id+"F2.wireOp",EDGE,"E2.top");var subQ4=sQuery(id+"F6.wireOp",EDGE,"E8");Q0=makeQuery(id+"F7.boolean.opBoolean","SPLIT",EDGE,{"disambiguationData":[TD([makeQuery(id+"F7.opExtrude","SWEPT_FACE",FACE,{"disambiguationData":[OSD([subQ4])]})])],"derivedFrom":makeQuery(id+"F3.opExtrude","SWEPT_EDGE",EDGE,{"disambiguationData":[OSD([subQ1,subQ2,subQ0])]})});}
            var Q1;
            {var subQ0=sQuery(id+"F2.wireOp",EDGE,"E2.top");var subQ1=sQuery(id+"F2.wireOp",EDGE,"E2.right");var subQ3=sQuery(id+"F6.wireOp",EDGE,"E9");var subQ4=sQuery(id+"F0.wireOp",EDGE,"E1.left");Q1=makeQuery(id+"F7.boolean.opBoolean","SPLIT",EDGE,{"disambiguationData":[TD([makeQuery(id+"F7.opExtrude","SWEPT_FACE",FACE,{"disambiguationData":[OSD([subQ3])]})])],"derivedFrom":makeQuery(id+"F3.opExtrude","SWEPT_EDGE",EDGE,{"disambiguationData":[OSD([subQ4,subQ0,subQ1])]})});}
            fillet(context, id + "F29", {"entities" : qUnion([Q0, Q1]), "radius" : 3.17 * mm, "tangentPropagation" : true, "allowEdgeOverflow" : false});
        }
        {
            var Q0;
            Q0=makeQuery(id+"F3.boolean.opBoolean","MERGE",EDGE,{"derivedFrom":[makeQuery(id+"F1.opExtrude","SWEPT_EDGE",EDGE,{"disambiguationData":[OSD([sQuery(id+"F0.wireOp",EDGE,"E0.top"),sQuery(id+"F0.wireOp",EDGE,"E0.left")])]}),makeQuery(id+"F3.opExtrude","SWEPT_EDGE",EDGE,{"disambiguationData":[OSD([sQuery(id+"F2.wireOp",EDGE,"E2.bottom"),sQuery(id+"F2.wireOp",EDGE,"E2.left")])]})]});
            fillet(context, id + "F30", {"entities" : qUnion([Q0]), "radius" : 3.17 * mm, "tangentPropagation" : true, "allowEdgeOverflow" : false});
        }
    });
